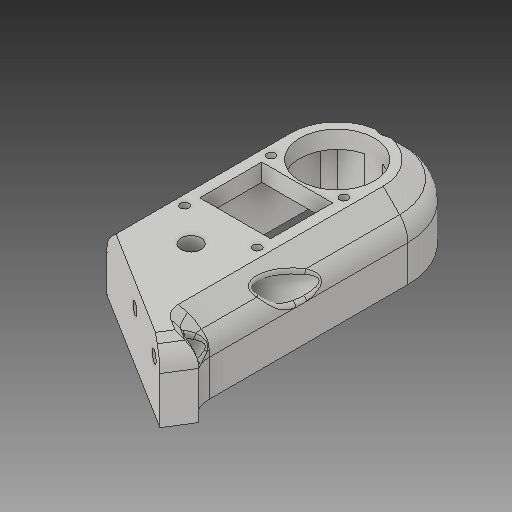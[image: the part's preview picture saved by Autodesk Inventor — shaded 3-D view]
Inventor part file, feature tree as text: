
AUTODESK INVENTOR PART (.ipt)
format: ipt  version: 2018 (Build 220112000, 112)  size: 830,976 bytes
history: native  units: mm
features: sketch x33, extrude x26, projected_geometry x23, fillet x9, hole x7, chamfer x5, other x3, mirror x1, plane x1, reference x1
ambient origin geometry x8: Origin, YZ Plane, XZ Plane, XY Plane, X Axis, Y Axis, Z Axis, Center Point
bodies: Solid1 (feature_tree)
feature tree (109):
  extrude  "Extrusion1"  Depth=45.0mm
  extrude  "Extrusion2"  Depth=1.95mm
  hole  "Hole1"  [1 undecoded]
  hole  "Hole2"  [1 undecoded]
  fillet  "Fillet1"  Radius=14.0mm
  extrude  "Extrusion3"  Depth=18.5mm
  extrude  "Extrusion4"  Depth=20.5mm
  extrude  "Extrusion5"  Depth=2.195mm
  extrude  "Extrusion6"  Depth=20.5mm
  hole  "Hole3"  [1 undecoded]
  extrude  "Extrusion7"  Depth=0.5mm
  extrude  "Extrusion8"  Depth=5.0mm TaperAngle=0.0deg
  extrude  "Extrusion9"  Depth=24.5mm
  extrude  "Extrusion10"  Depth=10.0mm
  extrude  "Extrusion11"  Depth=14.5mm
  extrude  "Extrusion12"  Depth=14.5mm
  extrude  "Extrusion13"  Depth=5.0mm
  extrude  "Extrusion14"  Depth=2.25mm
  extrude  "Extrusion15"  Depth=5.0mm
  extrude  "Extrusion16"  Depth=9.0mm
  extrude  "Extrusion17"  Depth=4.0mm
  chamfer  "Chamfer1"  Distance=1.0mm
  fillet  "Fillet7"  Radius=20.7mm
  fillet  "Fillet8"  Radius=32.0mm
  mirror  "Mirror1"
  extrude  "Extrusion18"  Depth=1.0mm TaperAngle=0.0deg
  extrude  "Extrusion19"  Depth=8.0mm
  extrude  "Extrusion20"  Depth=0.2mm TaperAngle=0.0deg
  extrude  "Extrusion21"  Depth=0.5mm TaperAngle=0.0deg
  extrude  "Extrusion22"  Depth=5.0mm TaperAngle=0.0deg
  extrude  "Extrusion23"  Depth=0.2mm TaperAngle=0.0deg
  chamfer  "Chamfer3"  Distance=0.2mm
  chamfer  "Chamfer4"  Distance=2.5mm Angle=45.0deg
  fillet  "Fillet12"  Radius=1.5mm
  fillet  "Fillet15"  Radius=0.5mm
  hole  "Hole6"  [1 undecoded]
  extrude  "Extrusion24"  Depth=25.0mm
  fillet  "Fillet16"  Radius=25.0mm
  chamfer  "Chamfer5"  Distance=25.0mm
  hole  "Hole7"  [1 undecoded]
  extrude  "Extrusion25"  Depth=2.0mm TaperAngle=0.0deg
  fillet  "Fillet18"  Radius=7.0mm
  fillet  "Fillet19"  Radius=4.0mm
  hole  "Hole8"  [1 undecoded]
  plane  "Work Plane1"
  hole  "Hole9"  [1 undecoded]
  fillet  "Fillet20"  Radius=4.9mm
  extrude  "Extrusion26"  Depth=4.9mm
  chamfer  "Chamfer6"  Distance=5.7mm
  sketch  "Sketch1"  dims[d0=24.5mm d1=45.0mm]
  sketch  "Sketch2"  dims[d2=1.95mm d3=0.0mm d4=2.25mm]
  projected_geometry  "Projected Loop1"
  sketch  "Sketch3"  dims[d5=20.0mm d6=2.25mm]
  projected_geometry  "Projected Loop2"
  sketch  "Sketch4"  dims[d7=5.25mm d8=5.25mm d9=14.0mm]
  projected_geometry  "Projected Loop3"
  sketch  "Sketch5"  dims[d10=5.25mm d11=18.5mm]
  projected_geometry  "Projected Loop4"
  sketch  "Sketch6"  dims[d12=10.0mm d13=0.0mm d14=20.5mm]
  projected_geometry  "Projected Loop5"
  sketch  "Sketch7"  dims[d15=2.0mm d16=2.195mm]
  projected_geometry  "Projected Loop6"
  sketch  "Sketch8"  dims[d17=2.0mm]
  projected_geometry  "Projected Loop7"
  sketch  "Sketch9"  dims[d18=2.4mm d19=6.0mm d20=4.4mm d21=2.0mm d22=90.0deg d23=8.0mm d24=20.594885mm d25=20.5mm]
  projected_geometry  "Projected Loop8"
  projected_geometry  "Projected Loop9"
  sketch  "Sketch10"  dims[d26=26.65mm d27=2.0mm]
  projected_geometry  "Projected Loop10"
  projected_geometry  "Projected Loop11"
  sketch  "Sketch11"  dims[d28=2.0mm]
  projected_geometry  "Projected Loop12"
  sketch  "Sketch12"  dims[d29=2.4mm d30=6.0mm d31=4.4mm d32=2.0mm d33=90.0deg d34=8.0mm d35=20.594885mm d36=0.5mm]
  sketch  "Sketch13"  dims[d37=18.0mm d38=5.0mm d39=0.0mm]
  sketch  "Sketch14"  dims[d41=10.0mm d42=0.0mm d43=24.5mm]
  projected_geometry  "Projected Loop13"
  sketch  "Sketch15"  dims[d44=1.15mm d45=0.0mm d46=10.0mm]
  sketch  "Sketch16"  dims[d47=21.0mm d48=14.5mm]
  projected_geometry  "Projected Loop14"
  sketch  "Sketch17"  dims[d49=20.0mm d50=14.5mm]
  projected_geometry  "Projected Loop15"
  sketch  "Sketch18"  dims[d51=24.5mm d52=5.0mm]
  projected_geometry  "Projected Loop16"
  sketch  "Sketch19"  dims[d53=5.0mm d54=2.25mm]
  projected_geometry  "Projected Loop17"
  sketch  "Sketch20"  dims[d55=2.25mm d56=5.0mm]
  projected_geometry  "Projected Loop18"
  sketch  "Sketch22"  dims[d57=5.0mm d58=9.0mm]
  sketch  "Sketch26"  dims[d59=14.75mm d60=4.0mm d61=1.0mm d62=0.0mm d63=20.7mm]
  sketch  "Sketch27"  dims[d64=2.4mm d65=6.0mm d66=4.4mm d67=2.0mm d68=90.0deg d69=8.0mm d70=20.594885mm d72=32.0mm]
  projected_geometry  "Projected Loop22"
  sketch  "Sketch28"  dims[d73=5.0mm d74=0.0mm d75=1.0mm d76=0.0mm]
  sketch  "Sketch29"  dims[d77=12.25mm d78=0.0mm d80=8.0mm]
  sketch  "Sketch31"  dims[d81=4.5mm d82=0.0mm d84=0.2mm d85=0.0mm]
  projected_geometry  "Projected Loop24"
  sketch  "Sketch32"  dims[d86=21.0mm d87=0.5mm d88=0.0mm]
  reference  "Reference1"
  sketch  "Sketch33"  dims[d91=8.0mm d92=0.0mm d93=5.0mm d94=0.0mm]
  sketch  "Sketch34"  dims[d95=5.0mm d96=0.0mm d98=0.2mm d99=0.0mm d100=0.2mm d101=0.0mm d102=2.5mm d103=2.0mm d104=45.0deg d105=1.5mm d114=0.5mm]
  projected_geometry  "Projected Loop25"
  sketch  "Sketch35"  dims[d115=22.55mm d116=0.0mm d128=40.0mm]
  sketch  "Sketch36"  dims[d129=70.0mm d130=25.0mm d131=25.0mm d132=0.0mm d133=25.0mm d134=0.0mm]
  projected_geometry  "Projected Loop26"
  sketch  "Sketch37"  dims[d135=25.0mm d136=0.0mm d137=2.0mm d138=0.0mm]
  sketch  "Sketch38"  dims[d143=8.0mm d144=2.0mm d145=0.0mm d148=7.0mm d149=2.0mm d150=45.0deg d152=4.0mm d153=2.0mm d154=45.0deg d155=8.0mm d158=8.0mm d159=4.9mm d160=4.9mm d161=3.2mm d162=6.0mm d163=6.3mm d164=2.0mm d165=90.0deg d166=8.0mm d167=20.594885mm d168=5.7mm d169=11.0mm d170=0.0mm d171=0.7mm d173=2.0mm d174=2.0mm d175=45.0deg d176=6.0mm d177=3.2mm d178=7.01mm d179=6.3mm d180=2.0mm d181=90.0deg d182=10.979mm d183=20.594885mm d184=5.7mm d185=11.0mm d186=0.0mm d187=1.5mm d188=1.5mm d189=14.0mm d190=17.0mm d191=5.0mm d192=3.3mm d193=6.0mm d194=3.023mm d195=2.0mm d196=14.3117mm d197=8.0mm d198=20.594885mm d199=-100.0mm d200=5.7mm d201=6.0mm d202=3.023mm d203=2.0mm d204=14.3117mm d205=96.0mm d206=0.0mm d207=1.0mm d208=16.0mm d209=2.0mm d210=0.0mm d211=1.5mm d212=2.0mm d213=45.0deg]
  projected_geometry  "Projected Loop27"
  parser-record x1  (decoder bookkeeping rows leaked as tree rows — omitted from the tree; the rows remain in map.json)
  other  "bottomarm.iam"
  other  "arm1:1"
note: 7 required parameter values undecoded (feature->parameter linkage not recoverable at this tier; creation-order binding heuristic only, values carry confidence <= 0.55)
note: 1 file-system path scrubbed to <path> (originals preserved in map.json)
